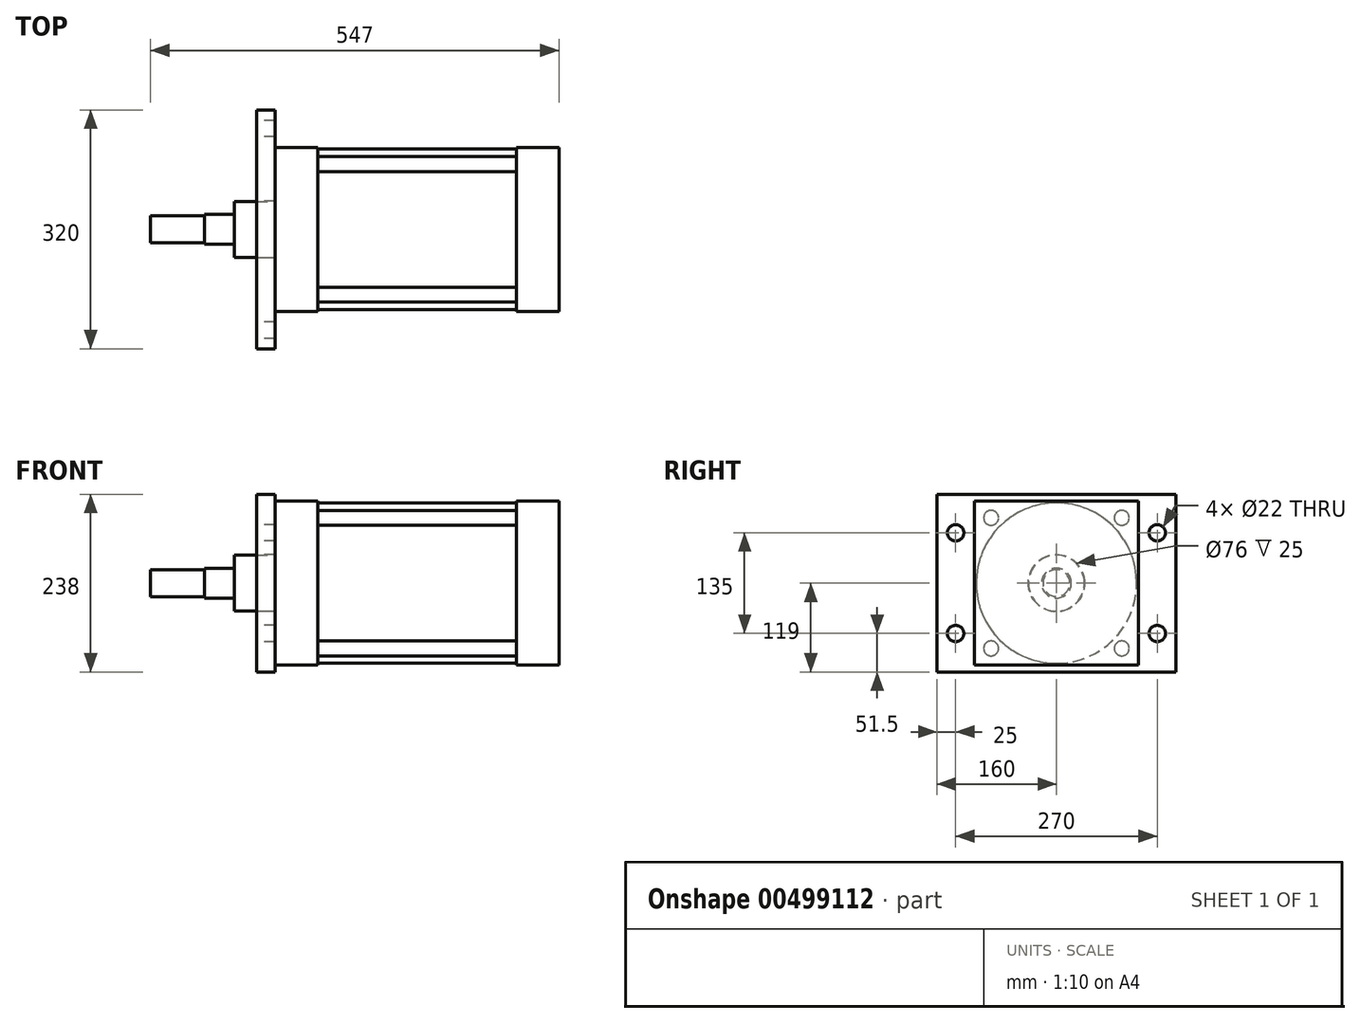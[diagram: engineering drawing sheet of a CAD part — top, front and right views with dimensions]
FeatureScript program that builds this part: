
annotation { "Feature Type Name" : "Feature", "Feature Type Description" : "" }
export const myFeature = defineFeature(function(context is Context, id is Id, definition is map)
    precondition{}
    {
        {
            var Q0;
            Q0=qCreatedBy(makeId("Right.planeOp"),FACE);
            var sketch = newSketch(context, id + "F0", { "sketchPlane" : qUnion([Q0])});
            skLineSegment(sketch, "E0.bottom", {"start": v(160, -119) * mm, "end": v(-160, -119) * mm});
            skLineSegment(sketch, "E0.top", {"start": v(160, 119) * mm, "end": v(-160, 119) * mm});
            skLineSegment(sketch, "E0.left", {"start": v(160, -119) * mm, "end": v(160, 119) * mm});
            skLineSegment(sketch, "E0.right", {"start": v(-160, -119) * mm, "end": v(-160, 119) * mm});
            skPoint(sketch, "E0.middle", {"position": v(0, 0) * mm});
            skCircle(sketch, "E1", {"center": v(135, 67.5) * mm, "radius": 11 * mm});
            skCircle(sketch, "E2.MirrorC", {"center": v(-135, 67.5) * mm, "radius": 11 * mm});
            skCircle(sketch, "E3.MirrorC", {"center": v(-135, -67.5) * mm, "radius": 11 * mm});
            skCircle(sketch, "E4.MirrorC", {"center": v(135, -67.5) * mm, "radius": 11 * mm});
            skCircle(sketch, "E5", {"center": v(0, 0) * mm, "radius": 38 * mm});
            skSolve(sketch);
        }
        {
            var Q0;
            Q0 = qSketchRegion(id + "F0", true);
            extrude(context, id + "F1", {"entities" : qUnion([Q0]), "depth" : 25 * mm});
        }
        {
            var Q0;
            Q0=qCreatedBy(makeId("Front.planeOp"),FACE);
            var sketch = newSketch(context, id + "F2", { "sketchPlane" : qUnion([Q0])});
            skLineSegment(sketch, "E6", {"start": v(25, 37.5) * mm, "end": v(-30, 37.5) * mm});
            skLineSegment(sketch, "E7", {"start": v(-30, 37.5) * mm, "end": v(-30, 20) * mm});
            skLineSegment(sketch, "E8", {"start": v(-30, 20) * mm, "end": v(-70, 20) * mm});
            skLineSegment(sketch, "E9", {"start": v(-70, 20) * mm, "end": v(-70, 18) * mm});
            skLineSegment(sketch, "E10", {"start": v(-70, 0) * mm, "end": v(25, 0) * mm, "construction": true});
            skLineSegment(sketch, "E11", {"start": v(25, 0) * mm, "end": v(25, 37.5) * mm});
            skLineSegment(sketch, "E12", {"start": v(-70, 18) * mm, "end": v(-142, 18) * mm});
            skLineSegment(sketch, "E13", {"start": v(-142, 18) * mm, "end": v(-142, 0) * mm});
            skLineSegment(sketch, "E14", {"start": v(25, 0) * mm, "end": v(-142, 0) * mm});
            skSolve(sketch);
        }
        {
            var Q0;
            Q0 = qSketchRegion(id + "F2", true);
            var Q1;
            Q1=sQuery(id+"F2.wireOp",EDGE,"E14");
            revolve(context, id + "F3", {"entities" : qUnion([Q0]), "axis" : qUnion([Q1]), "revolveType" : RevolveType.FULL});
        }
        {
            var Q0;
            Q0=makeQuery(id+"F3.opRevolve","SWEPT_FACE",FACE,{"disambiguationData":[OSD([sQuery(id+"F2.wireOp",EDGE,"E11")])]});
            var sketch = newSketch(context, id + "F4", { "sketchPlane" : qUnion([Q0])});
            skLineSegment(sketch, "E15.bottom", {"start": v(110, -110) * mm, "end": v(-110, -110) * mm});
            skLineSegment(sketch, "E15.top", {"start": v(110, 110) * mm, "end": v(-110, 110) * mm});
            skLineSegment(sketch, "E15.left", {"start": v(110, -110) * mm, "end": v(110, 110) * mm});
            skLineSegment(sketch, "E15.right", {"start": v(-110, -110) * mm, "end": v(-110, 110) * mm});
            skPoint(sketch, "E15.middle", {"position": v(0, 0) * mm});
            skSolve(sketch);
        }
        {
            var Q0;
            Q0 = qSketchRegion(id + "F4", true);
            extrude(context, id + "F5", {"entities" : qUnion([Q0]), "operationType" : NewBodyOperationType.ADD, "depth" : 380 * mm});
        }
        {
            var Q0;
            Q0=makeQuery(id+"F5.opExtrude","SWEPT_FACE",FACE,{"disambiguationData":[OSD([sQuery(id+"F4.wireOp",EDGE,"E15.right")])]});
            var sketch = newSketch(context, id + "F6", { "sketchPlane" : qUnion([Q0])});
            skLineSegment(sketch, "E16.bottom", {"start": v(82, 110) * mm, "end": v(348, 110) * mm});
            skLineSegment(sketch, "E16.top", {"start": v(82, -110) * mm, "end": v(348, -110) * mm});
            skLineSegment(sketch, "E16.left", {"start": v(82, 110) * mm, "end": v(82, -110) * mm});
            skLineSegment(sketch, "E16.right", {"start": v(348, 110) * mm, "end": v(348, -110) * mm});
            skSolve(sketch);
        }
        {
            var Q0;
            Q0 = qSketchRegion(id + "F6", true);
            extrude(context, id + "F7", {"entities" : qUnion([Q0]), "operationType" : NewBodyOperationType.REMOVE, "endBound" : BoundingType.THROUGH_ALL, "oppositeDirection" : true, "depth" : 25 * mm});
        }
        {
            var Q0;
            Q0=makeQuery(id+"F7.boolean.opBoolean","COPY",FACE,{"derivedFrom":makeQuery(id+"F7.opExtrude","SWEPT_FACE",FACE,{"disambiguationData":[OSD([sQuery(id+"F6.wireOp",EDGE,"E16.left")])]})});
            var sketch = newSketch(context, id + "F8", { "sketchPlane" : qUnion([Q0])});
            skCircle(sketch, "E17", {"center": v(0, 0) * mm, "radius": 107.5 * mm});
            skCircle(sketch, "E18", {"center": v(87.5, 87.5) * mm, "radius": 10 * mm});
            skCircle(sketch, "E19.MirrorC", {"center": v(87.5, -87.5) * mm, "radius": 10 * mm});
            skCircle(sketch, "E20.MirrorC", {"center": v(-87.5, 87.5) * mm, "radius": 10 * mm});
            skCircle(sketch, "E21.MirrorC", {"center": v(-87.5, -87.5) * mm, "radius": 10 * mm});
            skSolve(sketch);
        }
        {
            var Q0;
            Q0 = qSketchRegion(id + "F8", true);
            var Q1;
            Q1=makeQuery(id+"F7.boolean.opBoolean","COPY",FACE,{"derivedFrom":makeQuery(id+"F7.opExtrude","SWEPT_FACE",FACE,{"disambiguationData":[OSD([sQuery(id+"F6.wireOp",EDGE,"E16.right")])]})});
            extrude(context, id + "F9", {"entities" : qUnion([Q0]), "operationType" : NewBodyOperationType.ADD, "endBound" : BoundingType.UP_TO_SURFACE, "endBoundEntityFace" : qUnion([Q1]), "depth" : 25 * mm});
        }
    });
